# Revit family: Matrix MAF
name_source: partatom
category: Lighting Fixtures
units: mm (PartAtom-declared; Revit-internal decimal feet)

## family parameters
Cut with Voids When Loaded = No
Host = Face
Light Source = No
OmniClass Number = 23.80.70.14.14
OmniClass Title = Exterior Floodlights
Part Type = Normal
Room Calculation Point = No
Round Connector Dimension = Use Diameter
Shared = No

## types (7) — shared parameters
Apparent Load = 0 VA
Default Elevation = 48 "
Description = Matrix flood combines superior luminaire design with excellent versatility, performance and value
Glass = White Glass
Lamp = LED
Load Classification = Lighting
Manufacturer = Beacon Products
Model = Matrix MAF
Power Factor = 1
URL = https://www.currentlighting.com
Voltage = 120 V
Wattage Comments = 265W to 610W

## per-type parameters (varying)
| type | Angle | Assembly Code | Photometric Web Files | Product Material | zz Angle 1 |
| MAF-DB | 45.00° | D50 | Matrix : MAF-148L-380-5K7-W-U | Dark Bronze | 135.00° |
| MAF-BL | 75.00° |  | Matrix : MAF-192L-490-5K7-N-U | Black | 165.00° |
| MAF-WH | 75.00° |  | Matrix : MAF-192L-490-5K7-N-U | White | 165.00° |
| MAF-PS | 75.00° |  | Matrix : MAF-192L-490-5K7-N-U | Platinum | 165.00° |
| MAF-GYS | 75.00° |  | Matrix : MAF-192L-490-5K7-N-U | Light Grey | 165.00° |
| MAF-GT | 75.00° |  | Matrix : MAF-192L-490-5K7-N-U | Graphite | 165.00° |
| MAF-TT | 75.00° |  | Matrix : MAF-192L-490-5K7-N-U | Titanium | 165.00° |

## geometry (parser evidence)
native form markers: Blend x38, Sweep x10
no freeform markers — native parametric forms only
